# Revit family: Shower-Outlet-Caroma Tasman II-Hand
name_source: partatom
category: Plumbing Fixtures
revit_build: Autodesk Revit 2014 (Build: 20131024_2115(x64)
units: mm (PartAtom-declared; Revit-internal decimal feet)

## types (1)
- Standard
    Assembly Code = D2010710
    CW Connection = Yes
    CWFU = 2.37
    Connector Radius = 10 mm  [stored 0.0328084 ft]
    Cost = 0 $
    Default Elevation = 1800 mm  [stored 5.90551 ft]
    Description = Caroma Tasman II Hand Shower
    HW Connection = Yes
    HWFU = 2.37
    Manufacturer = GWA Bathrooms & Kitchens
    Material_ANZRS = Metal-Chrome-Caroma
    Model = 992546C3A
    ModifiedIssue_ANZRS = 20140716 $
    Pressure Drop = 0.00 psi
    Type Comments = Four Spray Options
    URL = http://www.caroma.com.au
    Vent Connection = No
    WELSRating_ANZRS = WELS 3 Star rated, 9L/min
    Waste Connection = No

note: [stored X ft] marks values corroborated as IEEE doubles in the binary element streams (Revit-internal decimal feet)

## geometry (parser evidence)
native form markers: Blend x10, Sweep x1
no freeform markers — native parametric forms only
